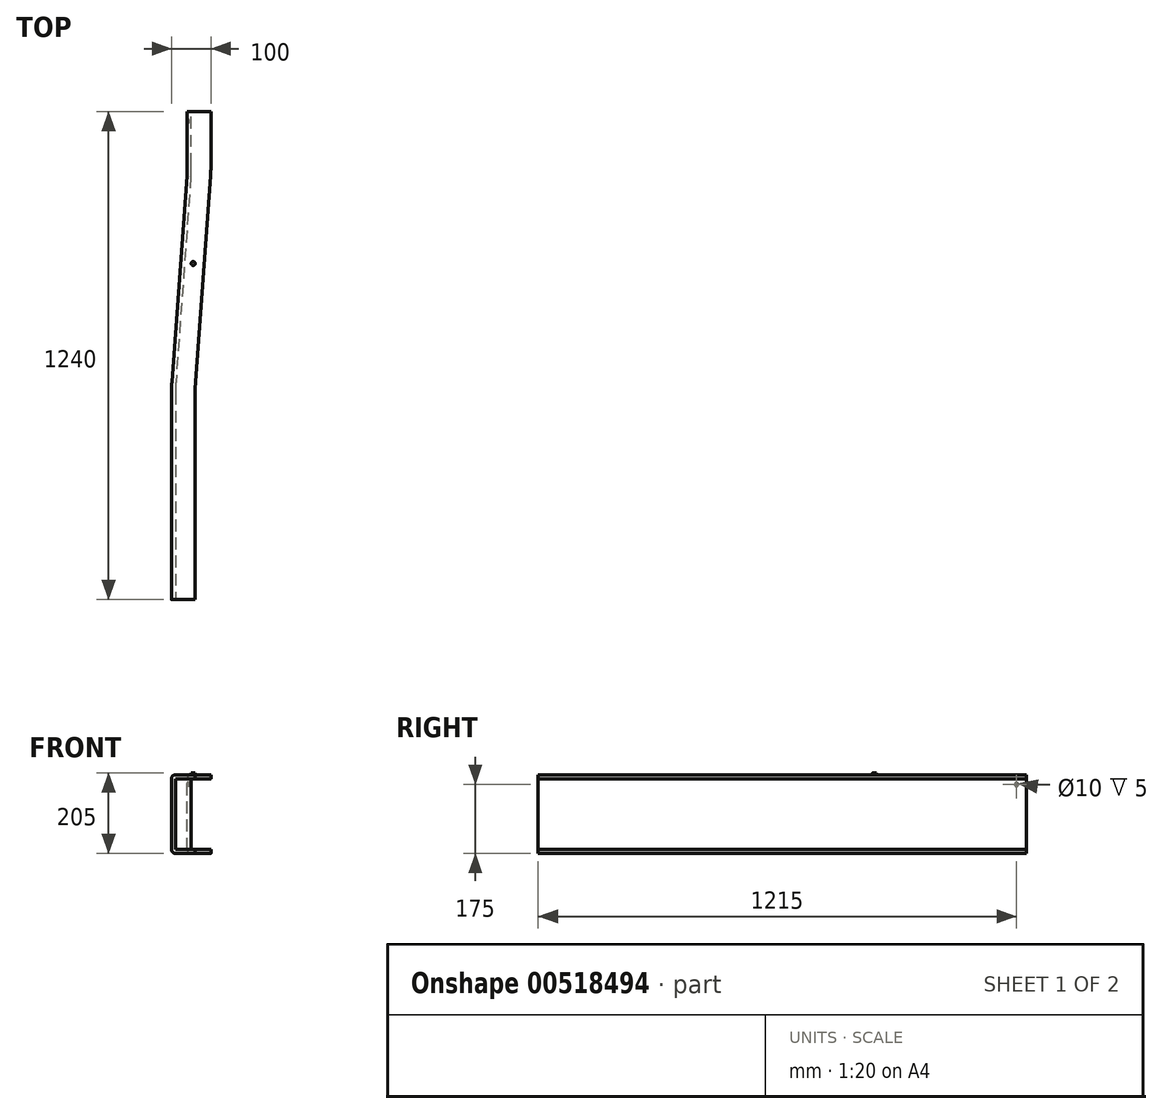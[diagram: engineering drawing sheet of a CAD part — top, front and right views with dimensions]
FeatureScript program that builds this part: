
annotation { "Feature Type Name" : "Feature", "Feature Type Description" : "" }
export const myFeature = defineFeature(function(context is Context, id is Id, definition is map)
    precondition{}
    {
        {
            var Q0;
            Q0=qCreatedBy(makeId("Top.planeOp"),FACE);
            var sketch = newSketch(context, id + "F0", { "sketchPlane" : qUnion([Q0])});
            skLineSegment(sketch, "E0", {"start": v(0, 0) * mm, "end": v(0, -150) * mm});
            skLineSegment(sketch, "E1", {"start": v(0, -150) * mm, "end": v(-40, -700) * mm});
            skLineSegment(sketch, "E2", {"start": v(-40, -700) * mm, "end": v(-40, -1240) * mm});
            skLineSegment(sketch, "E3", {"start": v(-40, -1240) * mm, "end": v(20, -1240) * mm});
            skLineSegment(sketch, "E4", {"start": v(20, -1240) * mm, "end": v(20, -700) * mm});
            skLineSegment(sketch, "E5", {"start": v(20, -700) * mm, "end": v(60, -150) * mm});
            skLineSegment(sketch, "E6", {"start": v(60, -150) * mm, "end": v(60, 0) * mm});
            skLineSegment(sketch, "E7", {"start": v(60, 0) * mm, "end": v(0, 0) * mm});
            skSolve(sketch);
        }
        {
            var Q0;
            Q0 = qSketchRegion(id + "F0", true);
            extrude(context, id + "F1", {"entities" : qUnion([Q0]), "oppositeDirection" : true, "depth" : 200 * mm, "offsetDistance" : 25 * mm});
        }
        {
            var Q0;
            Q0=makeQuery(id+"F1.opExtrude","SWEPT_EDGE",EDGE,{"disambiguationData":[OSD([sQuery(id+"F0.wireOp",EDGE,"E1"),sQuery(id+"F0.wireOp",EDGE,"E2")])]});
            var Q1;
            Q1=makeQuery(id+"F1.opExtrude","SWEPT_EDGE",EDGE,{"disambiguationData":[OSD([sQuery(id+"F0.wireOp",EDGE,"E0"),sQuery(id+"F0.wireOp",EDGE,"E1")])]});
            var Q2;
            Q2=makeQuery(id+"F1.opExtrude","SWEPT_EDGE",EDGE,{"disambiguationData":[OSD([sQuery(id+"F0.wireOp",EDGE,"E4"),sQuery(id+"F0.wireOp",EDGE,"E5")])]});
            var Q3;
            Q3=makeQuery(id+"F1.opExtrude","SWEPT_EDGE",EDGE,{"disambiguationData":[OSD([sQuery(id+"F0.wireOp",EDGE,"E5"),sQuery(id+"F0.wireOp",EDGE,"E6")])]});
            fillet(context, id + "F2", {"entities" : qUnion([Q0, Q1, Q2, Q3]), "radius" : 400 * mm, "tangentPropagation" : true, "allowEdgeOverflow" : false});
        }
        {
            var Q0;
            Q0=makeQuery(id+"F1.opExtrude","CAP_EDGE",EDGE,{"disambiguationData":[OSD([sQuery(id+"F0.wireOp",EDGE,"E1")])],"isStart":true});
            var Q1;
            Q1=makeQuery(id+"F1.opExtrude","CAP_EDGE",EDGE,{"disambiguationData":[OSD([sQuery(id+"F0.wireOp",EDGE,"E1")])],"isStart":false});
            fillet(context, id + "F3", {"entities" : qUnion([Q0, Q1]), "radius" : 10 * mm, "tangentPropagation" : true, "allowEdgeOverflow" : false});
        }
        {
            var Q0;
            Q0=makeQuery(id+"F1.opExtrude","SWEPT_FACE",FACE,{"disambiguationData":[OSD([sQuery(id+"F0.wireOp",EDGE,"E4")])]});
            var Q1;
            Q1=makeQuery(id+"F2.opFillet","BLEND_FACE",FACE,{"disambiguationData":[OSD([sQuery(id+"F0.wireOp",EDGE,"E4"),sQuery(id+"F0.wireOp",EDGE,"E5")])]});
            var Q2;
            Q2=makeQuery(id+"F1.opExtrude","SWEPT_FACE",FACE,{"disambiguationData":[OSD([sQuery(id+"F0.wireOp",EDGE,"E5")])]});
            var Q3;
            Q3=makeQuery(id+"F2.opFillet","BLEND_FACE",FACE,{"disambiguationData":[OSD([sQuery(id+"F0.wireOp",EDGE,"E5"),sQuery(id+"F0.wireOp",EDGE,"E6")])]});
            var Q4;
            Q4=makeQuery(id+"F1.opExtrude","SWEPT_FACE",FACE,{"disambiguationData":[OSD([sQuery(id+"F0.wireOp",EDGE,"E6")])]});
            var Q5;
            Q5=makeQuery(id+"F1.opExtrude","SWEPT_FACE",FACE,{"disambiguationData":[OSD([sQuery(id+"F0.wireOp",EDGE,"E7")])]});
            var Q6;
            Q6=makeQuery(id+"F1.opExtrude","SWEPT_FACE",FACE,{"disambiguationData":[OSD([sQuery(id+"F0.wireOp",EDGE,"E3")])]});
            shell(context, id + "F4", {"entities" : qUnion([Q0, Q1, Q2, Q3, Q4, Q5, Q6]), "thickness" : 10 * mm});
        }
        {
            var Q0;
            Q0=makeQuery(id+"F1.opExtrude","SWEPT_FACE",FACE,{"disambiguationData":[OSD([sQuery(id+"F0.wireOp",EDGE,"E0")])]});
            var sketch = newSketch(context, id + "F5", { "sketchPlane" : qUnion([Q0])});
            skCircle(sketch, "E8", {"center": v(25, -25) * mm, "radius": 5 * mm});
            skSolve(sketch);
        }
        {
            var Q0;
            Q0 = qSketchRegion(id + "F5", true);
            extrude(context, id + "F6", {"entities" : qUnion([Q0]), "operationType" : NewBodyOperationType.REMOVE, "oppositeDirection" : true, "depth" : 5 * mm, "offsetDistance" : 25 * mm});
        }
        {
            var Q0;
            Q0=makeQuery(id+"F1.opExtrude","CAP_FACE",FACE,{"disambiguationData":[OSD([sQuery(id+"F0.wireOp",EDGE,"E0"),sQuery(id+"F0.wireOp",EDGE,"E1"),sQuery(id+"F0.wireOp",EDGE,"E2"),sQuery(id+"F0.wireOp",EDGE,"E3"),sQuery(id+"F0.wireOp",EDGE,"E4"),sQuery(id+"F0.wireOp",EDGE,"E5"),sQuery(id+"F0.wireOp",EDGE,"E6"),sQuery(id+"F0.wireOp",EDGE,"E7")])],"isStart":true});
            var sketch = newSketch(context, id + "F7", { "sketchPlane" : qUnion([Q0])});
            skCircle(sketch, "E9", {"center": v(15, -386) * mm, "radius": 5 * mm});
            skSolve(sketch);
        }
        {
            var Q0;
            Q0=makeQuery(id+"F7.imprint","IMPRINT",FACE,{"disambiguationData":[TD([[makeQuery(id+"F7.imprint","IMPRINT",EDGE,{"derivedFrom":sQuery(id+"F7.wireOp",EDGE,"E9")}),1.0]])]});
            extrude(context, id + "F8", {"entities" : qUnion([Q0]), "operationType" : NewBodyOperationType.ADD, "depth" : 5 * mm, "offsetDistance" : 25 * mm});
        }
    });
